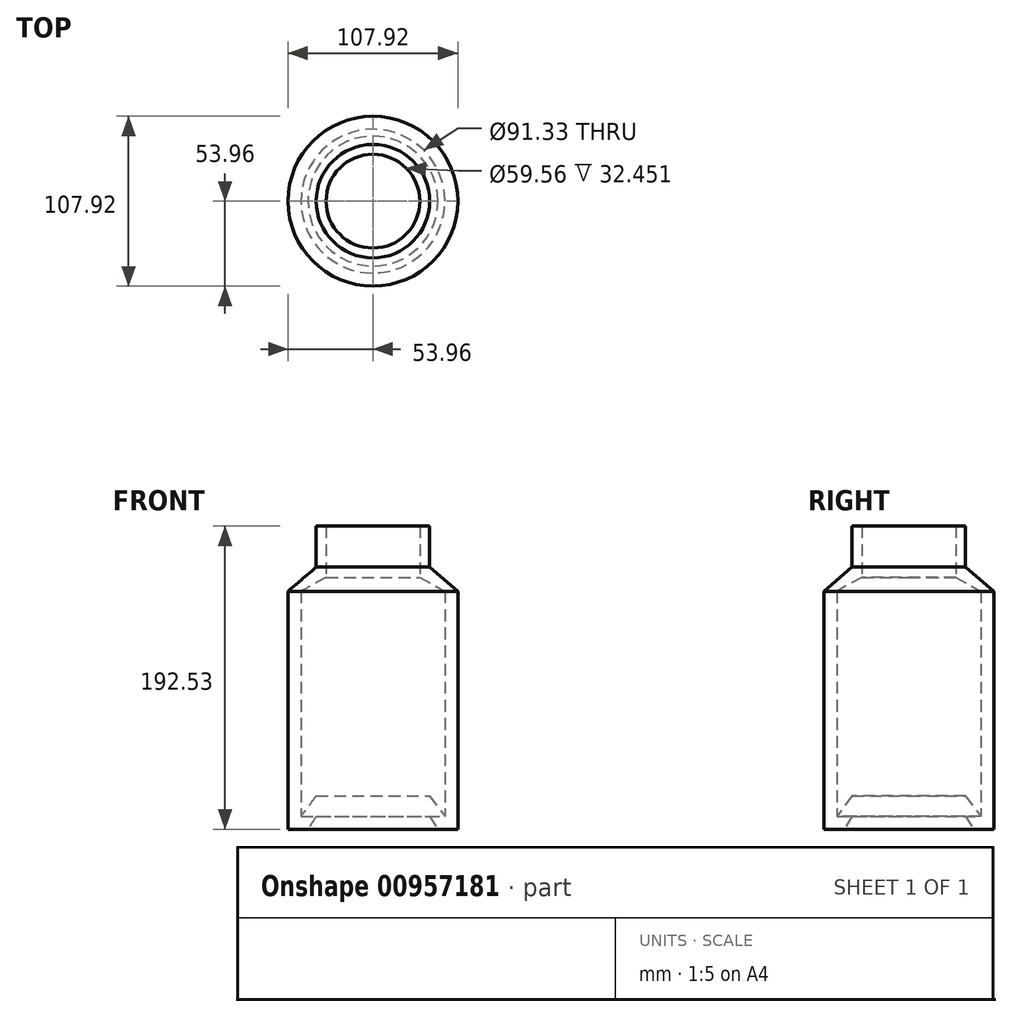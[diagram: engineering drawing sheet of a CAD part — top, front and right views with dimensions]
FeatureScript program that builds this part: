
annotation { "Feature Type Name" : "Feature", "Feature Type Description" : "" }
export const myFeature = defineFeature(function(context is Context, id is Id, definition is map)
    precondition{}
    {
        {
            var Q0;
            Q0=qCreatedBy(makeId("Front.planeOp"),FACE);
            var sketch = newSketch(context, id + "F0", { "sketchPlane" : qUnion([Q0])});
            skLineSegment(sketch, "E0", {"start": v(0, 0) * mm, "end": v(0, 71.41) * mm, "construction": true});
            skLineSegment(sketch, "E1", {"start": v(0, 0) * mm, "end": v(-36.02, 0) * mm});
            skLineSegment(sketch, "E2", {"start": v(-36.02, 0) * mm, "end": v(-41.25, -8.35) * mm});
            skLineSegment(sketch, "E3", {"start": v(-41.25, -8.35) * mm, "end": v(-53.96, -8.35) * mm});
            skLineSegment(sketch, "E4", {"start": v(-53.96, -8.35) * mm, "end": v(-53.96, 89.83) * mm});
            skLineSegment(sketch, "E5", {"start": v(-53.96, 89.83) * mm, "end": v(-53.96, 142.84) * mm});
            skLineSegment(sketch, "E6", {"start": v(-53.96, 142.84) * mm, "end": v(-36.02, 158.17) * mm});
            skLineSegment(sketch, "E7", {"start": v(-36.02, 158.17) * mm, "end": v(-36.02, 184.18) * mm});
            skLineSegment(sketch, "E8", {"start": v(-36.02, 184.18) * mm, "end": v(-29.78, 184.18) * mm});
            skLineSegment(sketch, "E9", {"start": v(-29.78, 184.18) * mm, "end": v(-29.78, 151.73) * mm});
            skLineSegment(sketch, "E10", {"start": v(-29.78, 151.73) * mm, "end": v(-45.67, 142.84) * mm});
            skLineSegment(sketch, "E11", {"start": v(-45.67, 142.84) * mm, "end": v(-45.67, 0) * mm});
            skLineSegment(sketch, "E12", {"start": v(-45.67, 0) * mm, "end": v(-36.02, 12.93) * mm});
            skLineSegment(sketch, "E13", {"start": v(-36.02, 12.93) * mm, "end": v(0, 12.93) * mm});
            skLineSegment(sketch, "E14", {"start": v(0, 12.93) * mm, "end": v(0, 0) * mm});
            skSolve(sketch);
        }
        {
            var Q0;
            Q0 = qSketchRegion(id + "F0", true);
            var Q1;
            Q1=sQuery(id+"F0.wireOp",EDGE,"E0");
            revolve(context, id + "F1", {"surfaceOperationType" : NewSurfaceOperationType.NEW, "entities" : qUnion([Q0]), "axis" : qUnion([Q1]), "revolveType" : RevolveType.FULL});
        }
    });
